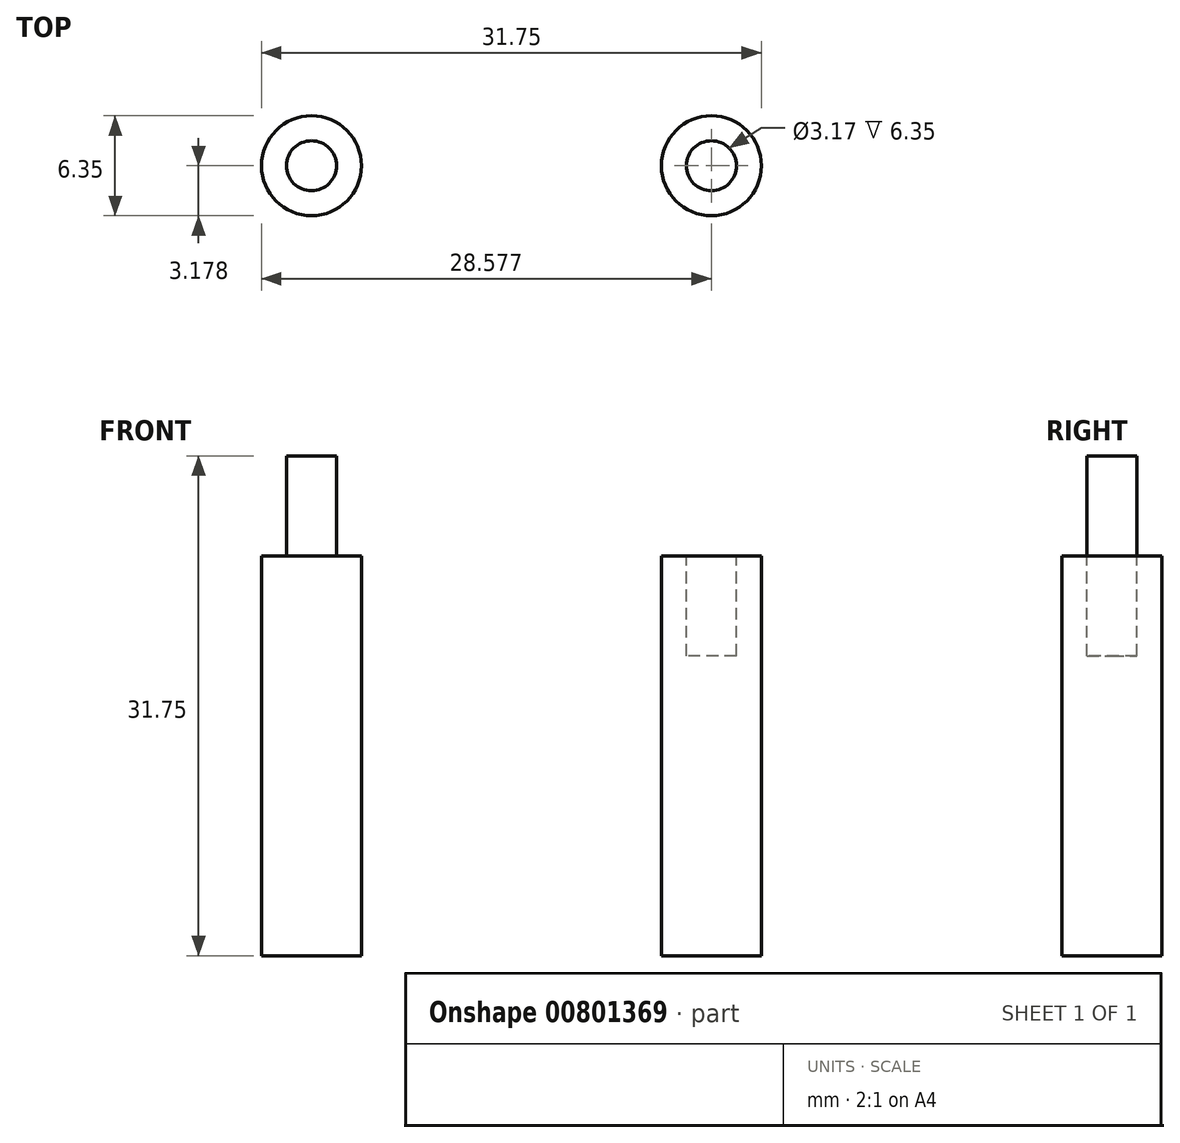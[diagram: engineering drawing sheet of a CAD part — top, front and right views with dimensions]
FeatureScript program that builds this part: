
annotation { "Feature Type Name" : "Feature", "Feature Type Description" : "" }
export const myFeature = defineFeature(function(context is Context, id is Id, definition is map)
    precondition{}
    {
        {
            var Q0;
            Q0=qCreatedBy(makeId("Top.planeOp"),FACE);
            var sketch = newSketch(context, id + "F0", { "sketchPlane" : qUnion([Q0])});
            skCircle(sketch, "E0", {"center": v(-9.92, -18.3) * mm, "radius": 3.18 * mm});
            skSolve(sketch);
        }
        {
            var Q0;
            Q0 = qSketchRegion(id + "F0", true);
            extrude(context, id + "F1", {"entities" : qUnion([Q0]), "depth" : 25.4 * mm, "offsetDistance" : 25.4 * mm});
        }
        {
            var Q0;
            Q0=makeQuery(id+"F1.opExtrude","SWEPT_BODY",BODY,{"disambiguationData":[OSD([sQuery(id+"F0.wireOp",EDGE,"E0")])]});
            var Q1;
            Q1=qCreatedBy(makeId("Right.planeOp"),FACE);
            transform(context, id + "F2", {"entities" : qUnion([Q0]), "transformType" : TransformType.TRANSLATION_DISTANCE, "transformDirection" : qUnion([Q1]), "distance" : 25.4 * mm, "makeCopy" : true});
        }
        {
            var Q0;
            Q0=makeQuery(id+"F1.opExtrude","CAP_FACE",FACE,{"disambiguationData":[OSD([sQuery(id+"F0.wireOp",EDGE,"E0")])],"isStart":false});
            var sketch = newSketch(context, id + "F3", { "sketchPlane" : qUnion([Q0])});
            skCircle(sketch, "E1", {"center": v(-9.92, -18.3) * mm, "radius": 1.59 * mm});
            skSolve(sketch);
        }
        {
            var Q0;
            Q0 = qSketchRegion(id + "F3", true);
            extrude(context, id + "F4", {"entities" : qUnion([Q0]), "operationType" : NewBodyOperationType.ADD, "depth" : 6.35 * mm, "offsetDistance" : 25.4 * mm});
        }
        {
            var Q0;
            Q0=makeQuery(id+"F2.opPattern","COPY",FACE,{"derivedFrom":makeQuery(id+"F1.opExtrude","CAP_FACE",FACE,{"disambiguationData":[OSD([sQuery(id+"F0.wireOp",EDGE,"E0")])],"isStart":false}),"instanceName":"1"});
            var sketch = newSketch(context, id + "F5", { "sketchPlane" : qUnion([Q0])});
            skCircle(sketch, "E2", {"center": v(15.48, -18.3) * mm, "radius": 1.59 * mm});
            skSolve(sketch);
        }
        {
            var Q0;
            Q0 = qSketchRegion(id + "F5", true);
            extrude(context, id + "F6", {"entities" : qUnion([Q0]), "operationType" : NewBodyOperationType.REMOVE, "oppositeDirection" : true, "depth" : 6.35 * mm, "offsetDistance" : 25.4 * mm});
        }
    });
